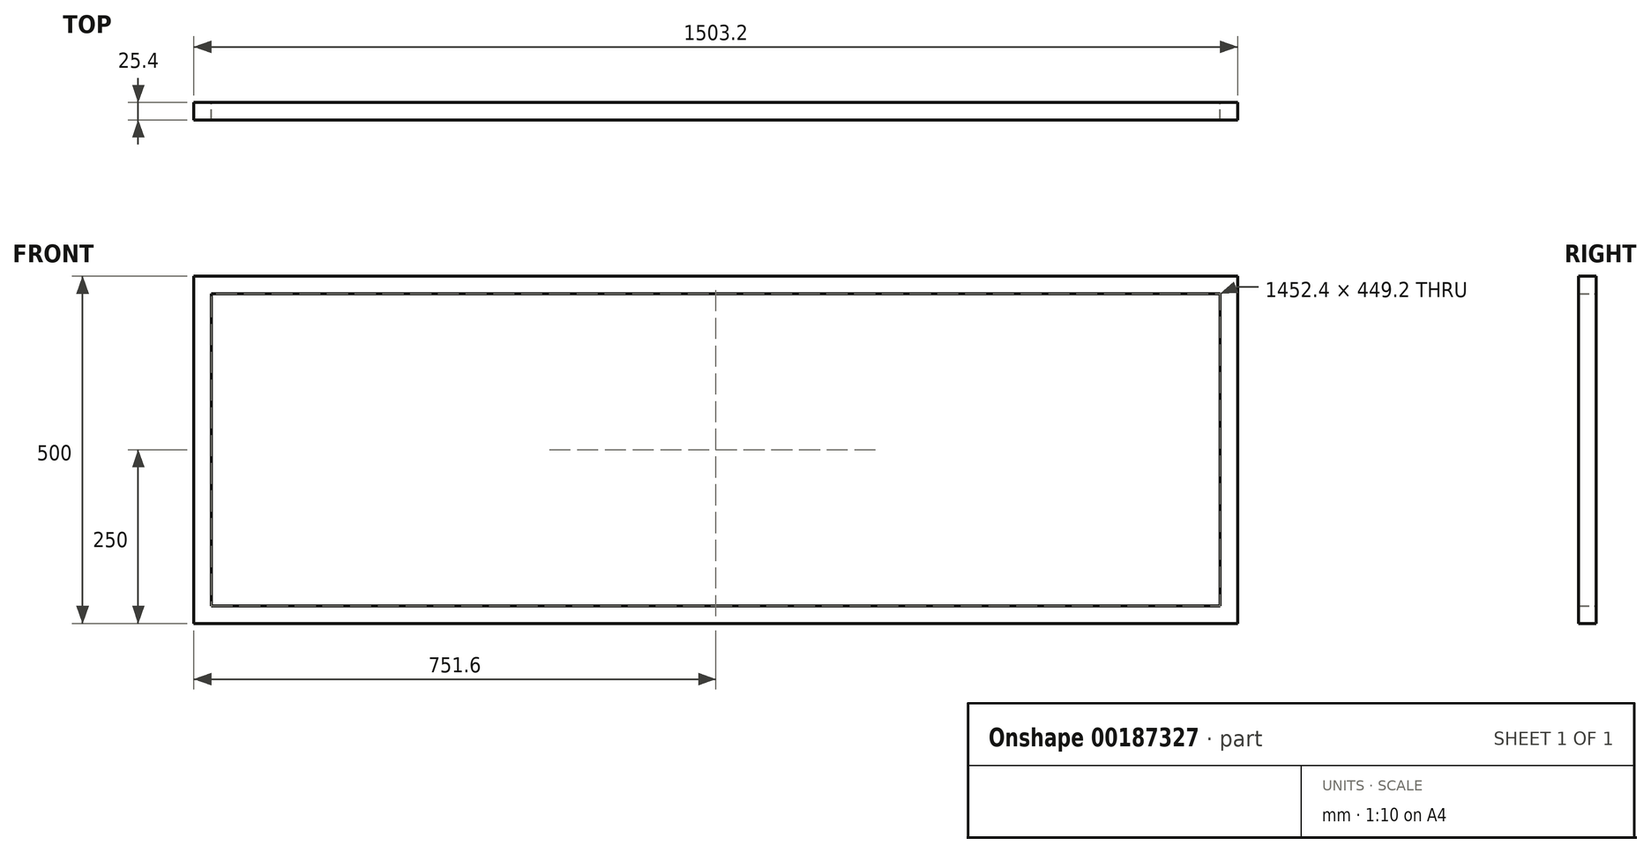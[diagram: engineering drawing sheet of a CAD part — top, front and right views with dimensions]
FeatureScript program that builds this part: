
annotation { "Feature Type Name" : "Feature", "Feature Type Description" : "" }
export const myFeature = defineFeature(function(context is Context, id is Id, definition is map)
    precondition{}
    {
        {
            var Q0;
            Q0=qCreatedBy(makeId("Front.planeOp"),FACE);
            var sketch = newSketch(context, id + "F0", { "sketchPlane" : qUnion([Q0])});
            skLineSegment(sketch, "E0.bottom", {"start": v(751.6, -250) * mm, "end": v(-751.6, -250) * mm});
            skLineSegment(sketch, "E0.top", {"start": v(751.6, 250) * mm, "end": v(-751.6, 250) * mm});
            skLineSegment(sketch, "E0.left", {"start": v(751.6, -250) * mm, "end": v(751.6, 250) * mm});
            skLineSegment(sketch, "E0.right", {"start": v(-751.6, -250) * mm, "end": v(-751.6, 250) * mm});
            skPoint(sketch, "E0.middle", {"position": v(0, 0) * mm});
            skLineSegment(sketch, "E1.0", {"start": v(-726.2, -224.6) * mm, "end": v(-726.2, 224.6) * mm});
            skLineSegment(sketch, "E1.1", {"start": v(726.2, -224.6) * mm, "end": v(-726.2, -224.6) * mm});
            skLineSegment(sketch, "E1.2", {"start": v(726.2, -224.6) * mm, "end": v(726.2, 224.6) * mm});
            skLineSegment(sketch, "E1.3", {"start": v(726.2, 224.6) * mm, "end": v(-726.2, 224.6) * mm});
            skSolve(sketch);
        }
        {
            var Q0;
            Q0=qSketchRegion(id+"F0",true);
            extrude(context, id + "F1", {"entities" : qUnion([Q0]), "depth" : 25.4 * mm});
        }
    });
